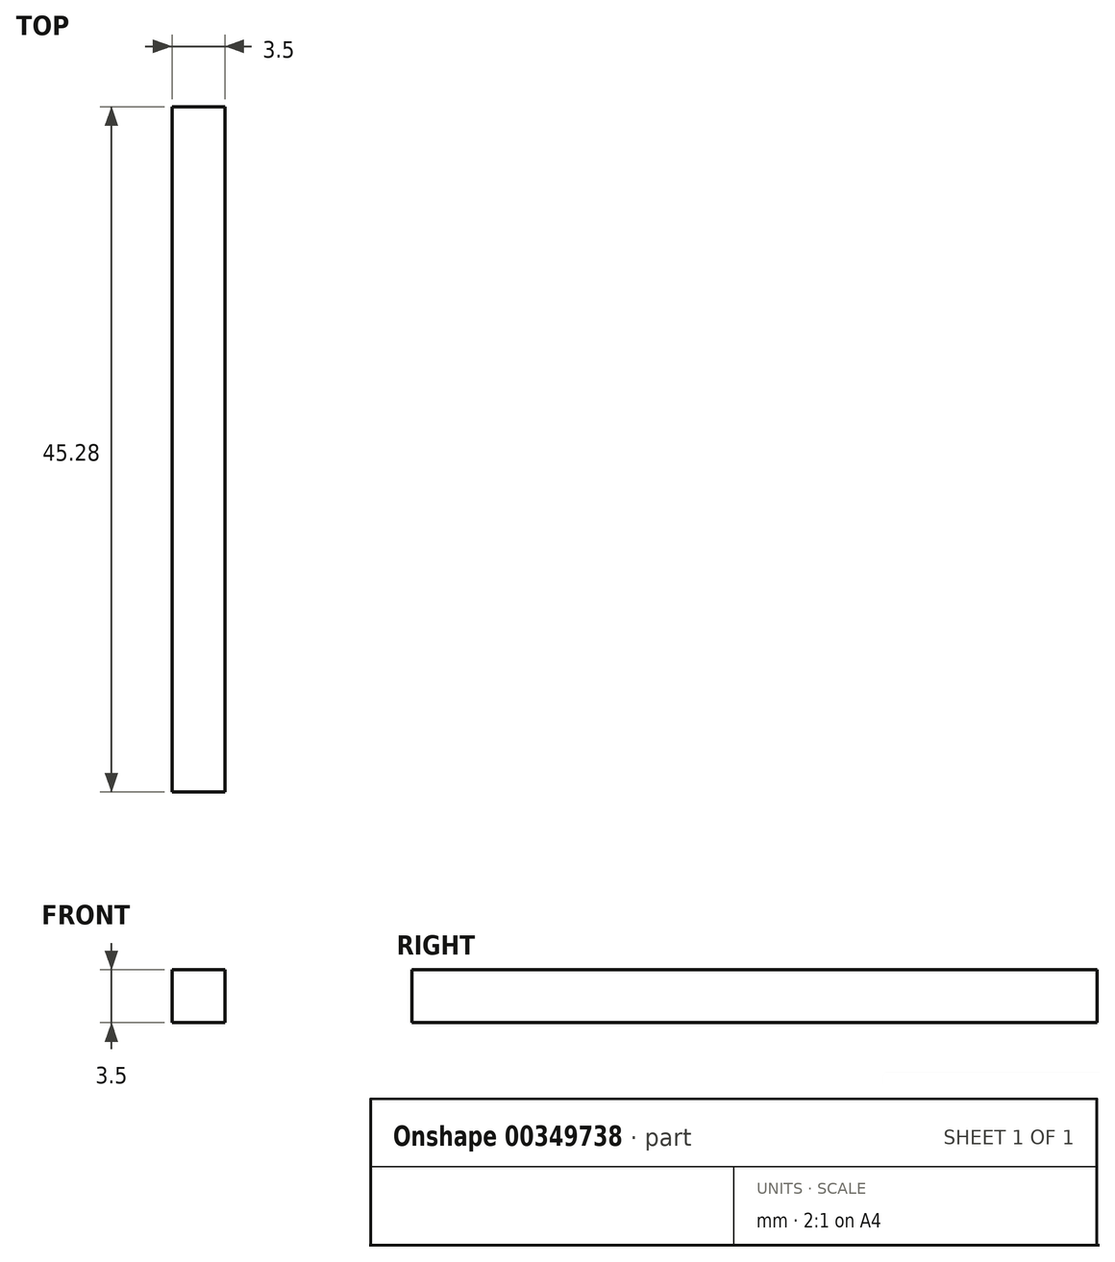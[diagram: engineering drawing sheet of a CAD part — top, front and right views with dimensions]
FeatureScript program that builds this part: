
annotation { "Feature Type Name" : "Feature", "Feature Type Description" : "" }
export const myFeature = defineFeature(function(context is Context, id is Id, definition is map)
    precondition{}
    {
        {
            var Q0;
            Q0=qCreatedBy(makeId("Top.planeOp"),FACE);
            var sketch = newSketch(context, id + "F0", { "sketchPlane" : qUnion([Q0])});
            skLineSegment(sketch, "E0.bottom", {"start": v(-1.75, 22.64) * mm, "end": v(1.75, 22.64) * mm});
            skLineSegment(sketch, "E0.top", {"start": v(-1.75, -22.64) * mm, "end": v(1.75, -22.64) * mm});
            skLineSegment(sketch, "E0.left", {"start": v(-1.75, 22.64) * mm, "end": v(-1.75, -22.64) * mm});
            skLineSegment(sketch, "E0.right", {"start": v(1.75, 22.64) * mm, "end": v(1.75, -22.64) * mm});
            skPoint(sketch, "E0.middle", {"position": v(0, 0) * mm});
            skSolve(sketch);
        }
        {
            var Q0;
            Q0=qSketchRegion(id+"F0",true);
            extrude(context, id + "F1", {"entities" : qUnion([Q0]), "depth" : 3.5 * mm});
        }
    });
